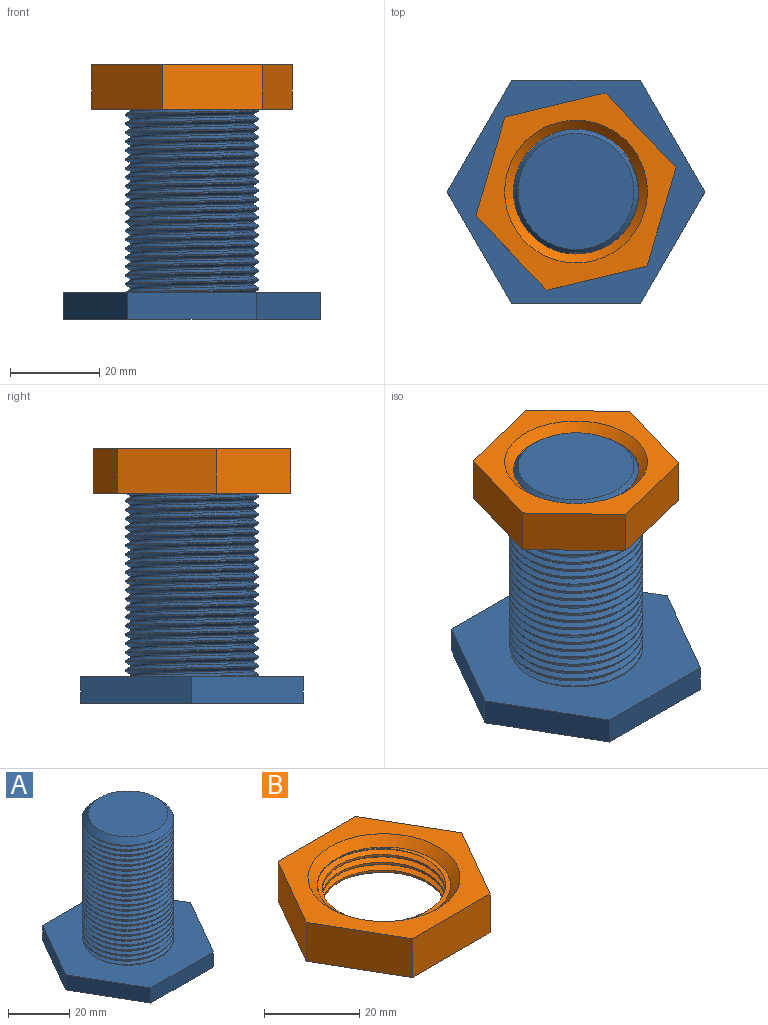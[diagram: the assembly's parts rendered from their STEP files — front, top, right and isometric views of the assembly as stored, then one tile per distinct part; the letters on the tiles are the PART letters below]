
ASSEMBLY  parts=2 mates=1
PART A: 15 faces, bbox 58.3x50.6x56.6 mm
  f0: plane 28.87x6mm, normal (0,1,0), area 173.2mm2, adj f1,f5,f6,f7
  f1: plane 25x14.43mm, normal (-0.87,0.5,0), area 173.2mm2, adj f0,f2,f6,f7
  f2: plane 25x14.43mm, normal (-0.87,-0.5,0), area 173.2mm2, adj f1,f3,f6,f7
  f3: plane 28.87x6mm, normal (0,-1,0), area 173.2mm2, adj f2,f4,f6,f7
  f4: plane 25x14.43mm, normal (0.87,-0.5,0), area 173.2mm2, adj f3,f5,f6,f7
  f5: plane 25x14.43mm, normal (0.87,0.5,0), area 173.2mm2, adj f0,f4,f6,f7
  f6: plane 58.33x50.59mm, normal (0,0,1), area 1515.6mm2, adj f0,f1,f2,f3,f4,f5,f8,f11
  f7: plane 57.74x50mm, normal (0,0,-1), area 2165.1mm2, adj f0,f1,f2,f3,f4,f5
  f8: cylinder r=15mm len=48mm, axis (0,0,-1), area 378.6mm2, adj f6,f10,f12,f13
  f9: plane 26x26mm, normal (0,0,1), area 530.9mm2, adj f10
  f10: cone r=13mm half-angle=45deg, axis (0,0,-1), area 248.8mm2, adj f8,f9,f14
  f11: bspline ~49.5x32.14mm, area 1168mm2, adj f6,f12,f13,f14
  f12: bspline ~49.63x34.64mm, area 2724.8mm2, adj f6,f8,f11,f14
  f13: bspline ~49.29x34.64mm, area 2730.3mm2, adj f6,f8,f11,f14
  f14: plane 30.59x30.59mm, normal (0,0,-1), area 57.3mm2, adj f10,f11,f12,f13
PART B: 18 faces, bbox 46.8x40.6x10.6 mm
  f0: plane 23.09x10mm, normal (0,1,0), area 230.9mm2, adj f1,f5,f6,f7
  f1: plane 20x11.55mm, normal (-0.87,0.5,0), area 230.9mm2, adj f0,f2,f6,f7
  f2: plane 20x11.55mm, normal (-0.87,-0.5,0), area 230.9mm2, adj f1,f3,f6,f7
  f3: plane 23.09x10mm, normal (0,-1,0), area 230.9mm2, adj f2,f4,f6,f7
  f4: plane 20x11.55mm, normal (0.87,-0.5,0), area 230.9mm2, adj f3,f5,f6,f7
  f5: plane 20x11.55mm, normal (0.87,0.5,0), area 230.9mm2, adj f0,f4,f6,f7
  f6: plane 46.19x40mm, normal (0,0,1), area 581.4mm2, adj f0,f1,f2,f3,f4,f5,f9
  f7: plane 46.19x40mm, normal (0,0,-1), area 581.4mm2, adj f0,f1,f2,f3,f4,f5,f8
  f8: cone r=16mm half-angle=45deg, axis (0,0,-1), area 266.6mm2, adj f7,f13,f15
  f9: cone r=14mm half-angle=45deg, axis (0,0,1), area 266.6mm2, adj f6,f14,f16
  f10: bspline ~32.52x28.17mm, area 319.2mm2, adj f12,f13,f14,f15,f16,f17
  f11: bspline ~32.52x28.17mm, area 319.2mm2, adj f12,f13,f14,f15,f16,f17
  f12: bspline ~32.73x28.35mm, area 77.1mm2, adj f10,f11,f13,f14
  f13: plane 10.54x10.36mm, normal (0,0,1), area 1.6mm2, adj f8,f10,f11,f12
  f14: plane 10.54x10.36mm, normal (0,0,-1), area 1.6mm2, adj f9,f10,f11,f12
  f15: plane 28.59x28.59mm, normal (0,0,-1), area 46mm2, adj f8,f10,f11,f17
  f16: plane 28.59x28.59mm, normal (0,0,1), area 46mm2, adj f9,f10,f11,f17
  f17: cylinder r=13mm len=26mm, axis (0,0,-1), area 122.9mm2, adj f10,f11,f15,f16
PLACE A t=(-19.56,-6.23,3.08)mm fixed
PLACE B rot(axis=(0,0,-1),166.5deg) t=(-77.9,-20.26,50.19)mm
MATE cylindrical A.f8 <-> B.f8  axis (0,0,1) through (-19.56,-6.23,59.08)mm
